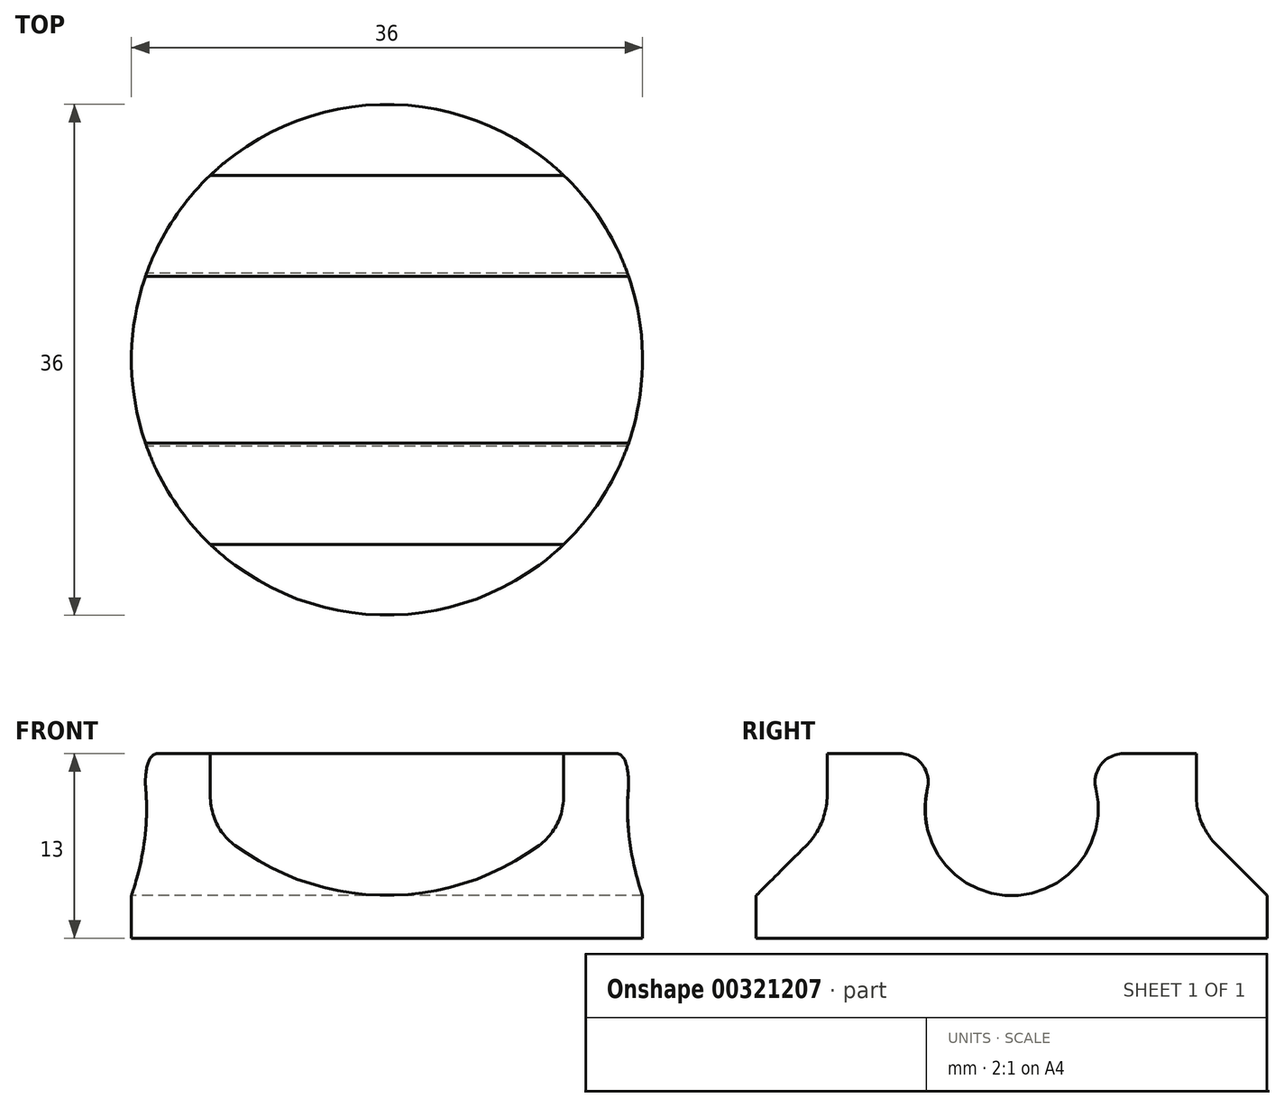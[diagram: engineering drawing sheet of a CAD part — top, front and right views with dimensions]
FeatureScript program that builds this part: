
annotation { "Feature Type Name" : "Feature", "Feature Type Description" : "" }
export const myFeature = defineFeature(function(context is Context, id is Id, definition is map)
    precondition{}
    {
        {
            var Q0;
            Q0=qCreatedBy(makeId("Top.planeOp"),FACE);
            var sketch = newSketch(context, id + "F0", { "sketchPlane" : qUnion([Q0])});
            skLineSegment(sketch, "E0.bottom", {"start": v(18, -13) * mm, "end": v(12.45, -13) * mm, "construction": true});
            skLineSegment(sketch, "E0.top", {"start": v(18, 13) * mm, "end": v(12.45, 13) * mm, "construction": true});
            skLineSegment(sketch, "E0.left", {"start": v(18, -13) * mm, "end": v(18, 13) * mm, "construction": true});
            skLineSegment(sketch, "E0.right", {"start": v(-18, -13) * mm, "end": v(-18, 13) * mm, "construction": true});
            skPoint(sketch, "E0.middle", {"position": v(0, 0) * mm});
            skArc(sketch, "E1", {"start": v(-12.45, 13) * mm, "mid": v(-18, 0) * mm, "end": v(-12.45, -13) * mm});
            skArc(sketch, "E2", {"start": v(12.45, 13) * mm, "mid": v(0, 18) * mm, "end": v(-12.45, 13) * mm});
            skLineSegment(sketch, "E3", {"start": v(12.45, 13) * mm, "end": v(-12.45, 13) * mm});
            skLineSegment(sketch, "E4", {"start": v(-12.45, 13) * mm, "end": v(-18, 13) * mm, "construction": true});
            skArc(sketch, "E5", {"start": v(-12.45, -13) * mm, "mid": v(13, -12.45) * mm, "end": v(12.45, 13) * mm});
            skLineSegment(sketch, "E6", {"start": v(12.45, -13) * mm, "end": v(-12.45, -13) * mm});
            skLineSegment(sketch, "E7", {"start": v(12.45, -13) * mm, "end": v(12.45, -13) * mm});
            skLineSegment(sketch, "E8", {"start": v(-12.45, -13) * mm, "end": v(-18, -13) * mm, "construction": true});
            skSolve(sketch);
        }
        {
            var Q0;
            Q0=makeQuery(id+"F0.imprint","IMPRINT",FACE,{"disambiguationData":[TD([[makeQuery(id+"F0.imprint","IMPRINT",EDGE,{"derivedFrom":sQuery(id+"F0.wireOp",EDGE,"E1")}),1.0]])]});
            var Q1;
            Q1=makeQuery(id+"F0.imprint","IMPRINT",FACE,{"disambiguationData":[TD([[makeQuery(id+"F0.imprint","IMPRINT",EDGE,{"derivedFrom":sQuery(id+"F0.wireOp",EDGE,"E2")}),1.0]])]});
            var Q2;
            {var subQ0=sQuery(id+"F0.wireOp",EDGE,"E6");Q2=makeQuery(id+"F0.imprint","IMPRINT",FACE,{"disambiguationData":[TD([[makeQuery(id+"F0.imprint","IMPRINT",EDGE,{"derivedFrom":subQ0}),1.0]])]});}
            extrude(context, id + "F1", {"entities" : qUnion([Q0, Q1, Q2]), "depth" : 3 * mm});
        }
        {
            var Q0;
            Q0=makeQuery(id+"F0.imprint","IMPRINT",FACE,{"disambiguationData":[TD([[makeQuery(id+"F0.imprint","IMPRINT",EDGE,{"derivedFrom":sQuery(id+"F0.wireOp",EDGE,"E1")}),1.0]])]});
            extrude(context, id + "F2", {"entities" : qUnion([Q0]), "operationType" : NewBodyOperationType.ADD, "depth" : (3 + 10) * mm});
        }
        {
            var Q0;
            Q0=qCreatedBy(makeId("Right.planeOp"),FACE);
            var sketch = newSketch(context, id + "F3", { "sketchPlane" : qUnion([Q0])});
            skPoint(sketch, "E9.0", {"position": v(13, 3) * mm});
            skPoint(sketch, "E9.1", {"position": v(-13, 3) * mm});
            skLineSegment(sketch, "E10", {"start": v(13, 3) * mm, "end": v(-13, 3) * mm, "construction": true});
            skCircle(sketch, "E11", {"center": v(0, 9.1) * mm, "radius": 6.1 * mm});
            skSolve(sketch);
        }
        {
            var Q0;
            Q0=makeQuery(id+"F3.imprint","IMPRINT",FACE,{"disambiguationData":[TD([[makeQuery(id+"F3.imprint","IMPRINT",EDGE,{"derivedFrom":sQuery(id+"F3.wireOp",EDGE,"E11")}),1.0]])]});
            var Q1;
            Q1=sQuery(id+"F3.wireOp",EDGE,"E11");
            extrude(context, id + "F4", {"entities" : qUnion([Q0]), "operationType" : NewBodyOperationType.REMOVE, "surfaceEntities" : qUnion([Q1]), "endBound" : BoundingType.SYMMETRIC, "depth" : 50 * mm});
        }
        {
            var Q0;
            Q0=makeQuery(id+"F2.boolean.opBoolean","INTERSECT",EDGE,{"derivedFrom":[makeQuery(id+"F1.opExtrude","CAP_FACE",FACE,{"disambiguationData":[OSD([sQuery(id+"F0.wireOp",EDGE,"E1"),sQuery(id+"F0.wireOp",EDGE,"E2"),sQuery(id+"F0.wireOp",EDGE,"E5")])],"isStart":false}),makeQuery(id+"F2.opExtrude","SWEPT_FACE",FACE,{"disambiguationData":[OSD([sQuery(id+"F0.wireOp",EDGE,"E3")])]})]});
            var Q1;
            Q1=makeQuery(id+"F2.boolean.opBoolean","INTERSECT",EDGE,{"derivedFrom":[makeQuery(id+"F1.opExtrude","CAP_FACE",FACE,{"disambiguationData":[OSD([sQuery(id+"F0.wireOp",EDGE,"E1"),sQuery(id+"F0.wireOp",EDGE,"E2"),sQuery(id+"F0.wireOp",EDGE,"E5")])],"isStart":false}),makeQuery(id+"F2.opExtrude","SWEPT_FACE",FACE,{"disambiguationData":[OSD([sQuery(id+"F0.wireOp",EDGE,"E6")])]})]});
            chamfer(context, id + "F5", {"entities" : qUnion([Q0, Q1]), "width" : 5 * mm, "tangentPropagation" : true});
        }
        {
            var Q0;
            Q0=makeQuery(id+"F4.boolean.opBoolean","INTERSECT",EDGE,{"disambiguationData":[OD(0.0)],"derivedFrom":[makeQuery(id+"F2.opExtrude","CAP_FACE",FACE,{"disambiguationData":[OSD([sQuery(id+"F0.wireOp",EDGE,"E1"),sQuery(id+"F0.wireOp",EDGE,"E3"),sQuery(id+"F0.wireOp",EDGE,"E5"),sQuery(id+"F0.wireOp",EDGE,"E6")])],"isStart":false}),makeQuery(id+"F4.opExtrude","SWEPT_FACE",FACE,{"disambiguationData":[OSD([sQuery(id+"F3.wireOp",EDGE,"E11")])]})]});
            var Q1;
            Q1=makeQuery(id+"F4.boolean.opBoolean","INTERSECT",EDGE,{"disambiguationData":[OD(1.0)],"derivedFrom":[makeQuery(id+"F2.opExtrude","CAP_FACE",FACE,{"disambiguationData":[OSD([sQuery(id+"F0.wireOp",EDGE,"E1"),sQuery(id+"F0.wireOp",EDGE,"E3"),sQuery(id+"F0.wireOp",EDGE,"E5"),sQuery(id+"F0.wireOp",EDGE,"E6")])],"isStart":false}),makeQuery(id+"F4.opExtrude","SWEPT_FACE",FACE,{"disambiguationData":[OSD([sQuery(id+"F3.wireOp",EDGE,"E11")])]})]});
            fillet(context, id + "F6", {"entities" : qUnion([Q0, Q1]), "radius" : 2 * mm, "tangentPropagation" : true, "allowEdgeOverflow" : false});
        }
        {
            var Q0;
            {var subQ0=makeQuery(id+"F2.opExtrude","SWEPT_FACE",FACE,{"disambiguationData":[OSD([sQuery(id+"F0.wireOp",EDGE,"E6")])]});Q0=makeQuery(id+"F5.opChamfer","BLEND_EDGE",EDGE,{"blendedFrom":[makeQuery(id+"F2.boolean.opBoolean","INTERSECT",EDGE,{"derivedFrom":[makeQuery(id+"F1.opExtrude","CAP_FACE",FACE,{"disambiguationData":[OSD([sQuery(id+"F0.wireOp",EDGE,"E1"),sQuery(id+"F0.wireOp",EDGE,"E2"),sQuery(id+"F0.wireOp",EDGE,"E5")])],"isStart":false}),subQ0]}),subQ0],"blendedInto":[subQ0]});}
            var Q1;
            {var subQ0=makeQuery(id+"F2.opExtrude","SWEPT_FACE",FACE,{"disambiguationData":[OSD([sQuery(id+"F0.wireOp",EDGE,"E3")])]});Q1=makeQuery(id+"F5.opChamfer","BLEND_EDGE",EDGE,{"blendedFrom":[makeQuery(id+"F2.boolean.opBoolean","INTERSECT",EDGE,{"derivedFrom":[makeQuery(id+"F1.opExtrude","CAP_FACE",FACE,{"disambiguationData":[OSD([sQuery(id+"F0.wireOp",EDGE,"E1"),sQuery(id+"F0.wireOp",EDGE,"E2"),sQuery(id+"F0.wireOp",EDGE,"E5")])],"isStart":false}),subQ0]}),subQ0],"blendedInto":[subQ0]});}
            fillet(context, id + "F7", {"entities" : qUnion([Q0, Q1]), "radius" : 5 * mm, "tangentPropagation" : true, "allowEdgeOverflow" : false});
        }
    });
